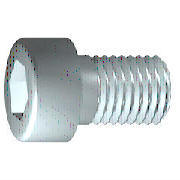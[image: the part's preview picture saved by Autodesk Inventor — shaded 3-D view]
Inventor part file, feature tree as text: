
AUTODESK INVENTOR PART (.ipt)
format: ipt  version: 2022 (Build 260153000, 153)  size: 189,440 bytes
history: native  units: mm (DEFAULTED — no unit token found)
features: sketch x2, other x1, extrude x1, plane x1, fillet x1
ambient origin geometry x7: Origin, YZ Plane, XY Plane, X Axis, Y Axis, Z Axis, Center Point
bodies: Solid1 (feature_tree)
feature tree (6):
  other  "Cuerpo"
  extrude  "Ranura"  Depth=4.0mm
  plane  "Work Plane1"
  fillet  "Fillet2"  Radius=4.0mm
  sketch  "Boceto1"  dims[d1=23.25mm d2=0.429515mm d3=4.0mm]
  sketch  "Boceto2"  dims[d4=2.0mm d5=60.0deg d6=4.0mm d7=4.0mm d8=3.464102mm d9=7.0mm d10=90.0deg d11=10.0mm d12=0.0mm d13=23.25mm d14=0.0mm d15=0.429415mm d16=0.429415mm d17=0.4mm d19=0.0mm d26=25.0mm d27=45.0deg d28=0.0mm d29=0.0mm d30=0.1mm]
